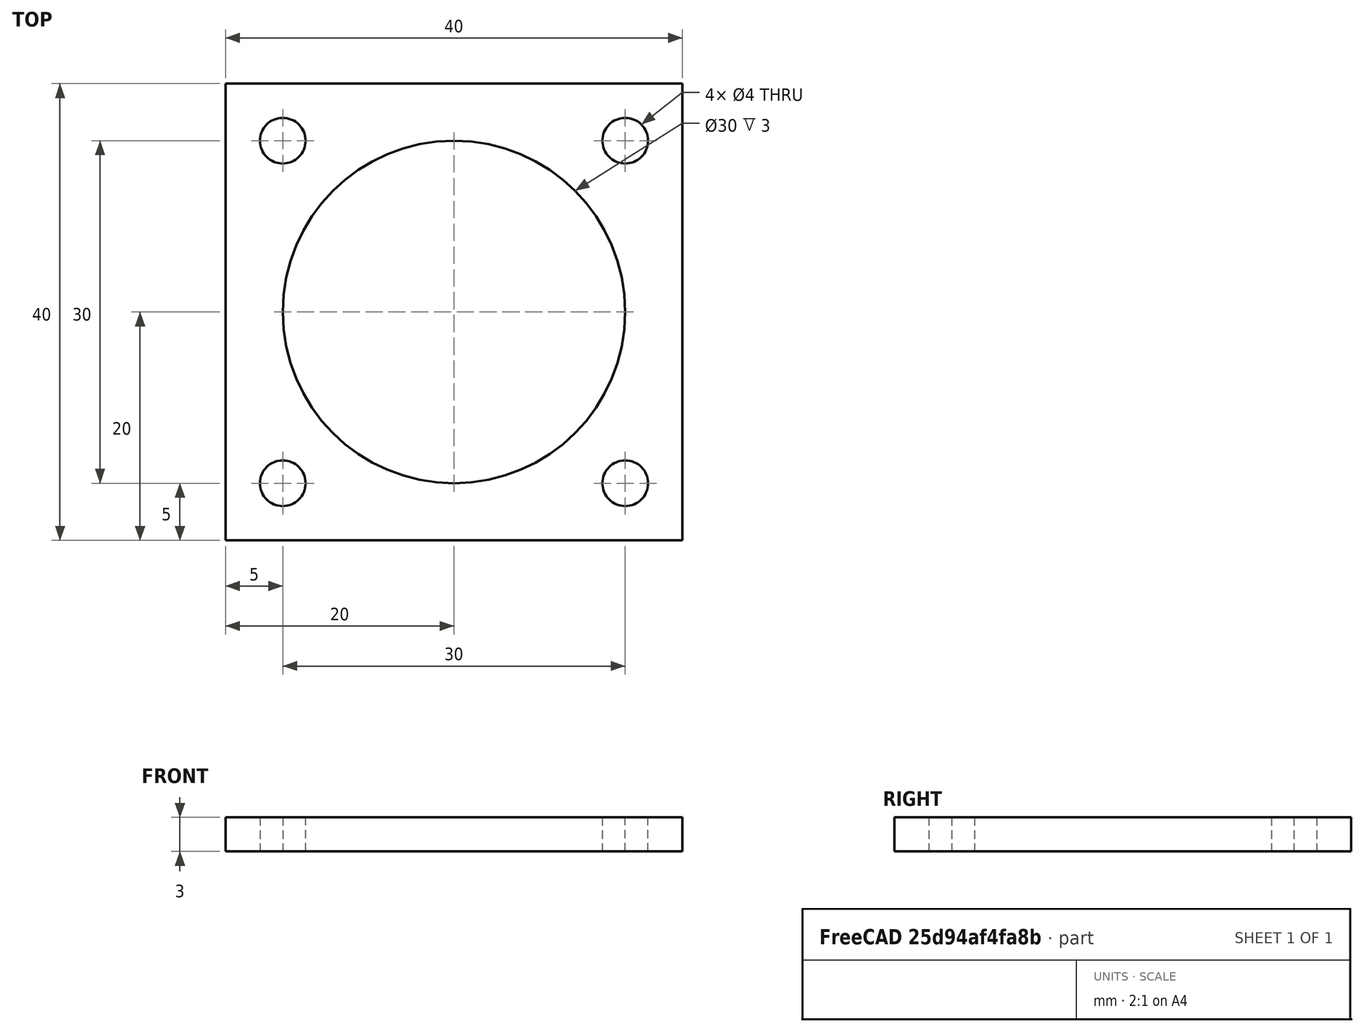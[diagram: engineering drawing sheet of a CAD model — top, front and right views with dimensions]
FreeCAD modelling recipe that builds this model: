
FCSTD DOCUMENT  (FreeCAD 0.16R6707 (Git))
Label: 06-01-placa-taladros
License: All rights reserved
LicenseURL: http://en.wikipedia.org/wiki/All_rights_reserved
objects: Sketcher::SketchObject×1, PartDesign::Pad×1
note: 3 computed .brp shape members not serialized (recipe doc carries the construction recipe); baked Part::Feature solids carry a one-line shape summary decoded from their .brp

FEATURE [Sketcher::SketchObject] Sketch  label="Plano-pieza"
  expr: Constraints.lado = 10mm * 4
  sketch-geometry (9):
    g0: LineSegment StartX=-20 StartY=20 StartZ=0 EndX=20 EndY=20 EndZ=0
    g1: LineSegment StartX=20 StartY=20 StartZ=0 EndX=20 EndY=-20 EndZ=0
    g2: LineSegment StartX=20 StartY=-20 StartZ=0 EndX=-20 EndY=-20 EndZ=0
    g3: LineSegment StartX=-20 StartY=-20 StartZ=0 EndX=-20 EndY=20 EndZ=0
    g4: Circle CenterX=-15 CenterY=15 CenterZ=0 NormalX=0 NormalY=0 NormalZ=1 Radius=2
    g5: Circle CenterX=-15 CenterY=-15 CenterZ=0 NormalX=0 NormalY=0 NormalZ=1 Radius=2
    g6: Circle CenterX=15 CenterY=-15 CenterZ=0 NormalX=0 NormalY=0 NormalZ=1 Radius=2
    g7: Circle CenterX=15 CenterY=15 CenterZ=0 NormalX=0 NormalY=0 NormalZ=1 Radius=2
    g8: Circle CenterX=0 CenterY=0 CenterZ=0 NormalX=0 NormalY=0 NormalZ=1 Radius=15
  constraints (22):
    c: Coincident(g0,g1)
    c: Coincident(g1,g2)
    c: Coincident(g2,g3)
    c: Coincident(g3,g0)
    c: Horizontal(g0)
    c: Horizontal(g2)
    c: Vertical(g1)
    c: Vertical(g3)
    c: Symmetric(g0,g1,g-1)
    c: Equal(g0,g1)
    c: DistanceX(g0,g4) = 5
    c: DistanceY(g4,g0) = 5
    c: Radius(g4) = 2
    c: Symmetric(g4,g7,g-2)
    c: Symmetric(g4,g5,g-1)
    c: Symmetric(g5,g6,g-2)
    c: Equal(g4,g5)
    c: Equal(g5,g6)
    c: Equal(g6,g7)
    c: DistanceX(g0,g0) = 40  'lado'
    c: Radius(g8) = 15
    c: Coincident(g8,g-1)
FEATURE [PartDesign::Pad] Pad  label="Pieza"
  Length = 3
  Length2 = 100
  Sketch = -> Sketch
  Type = 0
